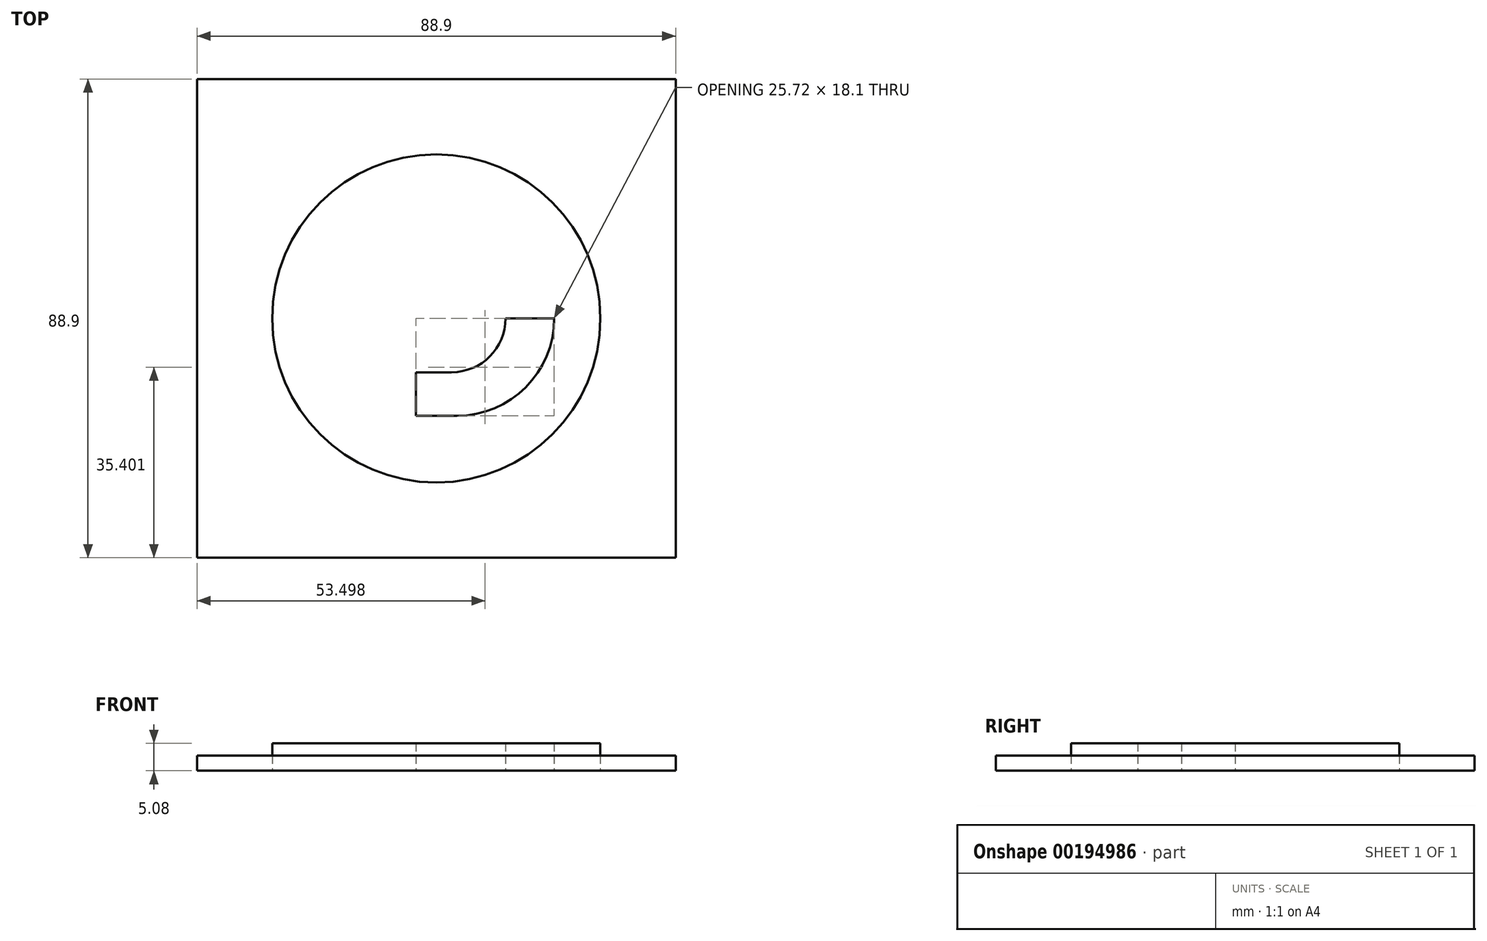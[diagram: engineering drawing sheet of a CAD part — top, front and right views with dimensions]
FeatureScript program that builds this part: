
annotation { "Feature Type Name" : "Feature", "Feature Type Description" : "" }
export const myFeature = defineFeature(function(context is Context, id is Id, definition is map)
    precondition{}
    {
        {
            var Q0;
            Q0=qCreatedBy(makeId("Top.planeOp"),FACE);
            var sketch = newSketch(context, id + "F0", { "sketchPlane" : qUnion([Q0])});
            skCircle(sketch, "E0", {"center": v(-1.1, 0) * mm, "radius": 38.1 * mm});
            skCircle(sketch, "E1", {"center": v(-1.1, 0) * mm, "radius": 30.48 * mm});
            skLineSegment(sketch, "E2", {"start": v(-4.91, -18.1) * mm, "end": v(-4.91, 7.14) * mm});
            skLineSegment(sketch, "E3", {"start": v(-4.91, 7.14) * mm, "end": v(-13, 7.14) * mm});
            skLineSegment(sketch, "E4", {"start": v(-13, 7.14) * mm, "end": v(-13, -18.1) * mm});
            skLineSegment(sketch, "E5", {"start": v(-13, -18.1) * mm, "end": v(-4.91, -18.1) * mm});
            skArc(sketch, "E6", {"start": v(20.8, 0) * mm, "mid": v(15.5, -12.8) * mm, "end": v(2.7, -18.1) * mm});
            skLineSegment(sketch, "E7", {"start": v(2.7, -18.1) * mm, "end": v(-4.91, -18.1) * mm});
            skLineSegment(sketch, "E8", {"start": v(-4.91, -18.1) * mm, "end": v(-4.91, -10) * mm});
            skLineSegment(sketch, "E9", {"start": v(-4.91, -10) * mm, "end": v(1.76, -10) * mm});
            skArc(sketch, "E10", {"start": v(1.76, -10) * mm, "mid": v(8.83, -7.07) * mm, "end": v(11.76, 0) * mm});
            skLineSegment(sketch, "E11", {"start": v(11.76, 0) * mm, "end": v(20.8, 0) * mm});
            skArc(sketch, "E12", {"start": v(20.8, 0) * mm, "mid": v(15.5, 12.8) * mm, "end": v(2.7, 18.1) * mm});
            skLineSegment(sketch, "E13", {"start": v(2.7, 18.1) * mm, "end": v(-22.06, 18.1) * mm});
            skLineSegment(sketch, "E14", {"start": v(-22.06, 18.1) * mm, "end": v(-22.06, 10) * mm});
            skLineSegment(sketch, "E15", {"start": v(-22.06, 10) * mm, "end": v(1.76, 10) * mm});
            skArc(sketch, "E16", {"start": v(1.76, 10) * mm, "mid": v(8.83, 7.07) * mm, "end": v(11.76, 0) * mm});
            skSolve(sketch);
        }
        {
            var Q0;
            Q0=makeQuery(id+"F0.imprint","IMPRINT",FACE,{"disambiguationData":[TD([[makeQuery(id+"F0.imprint","IMPRINT",EDGE,{"derivedFrom":sQuery(id+"F0.wireOp",EDGE,"E2")}),1.0]])]});
            var Q1;
            Q1=makeQuery(id+"F0.imprint","IMPRINT",FACE,{"disambiguationData":[TD([[makeQuery(id+"F0.imprint","IMPRINT",EDGE,{"derivedFrom":sQuery(id+"F0.wireOp",EDGE,"E12")}),1.0]])]});
            var Q2;
            Q2=makeQuery(id+"F0.imprint","IMPRINT",FACE,{"disambiguationData":[TD([[makeQuery(id+"F0.imprint","IMPRINT",EDGE,{"derivedFrom":sQuery(id+"F0.wireOp",EDGE,"E6")}),-1.0]])]});
            var Q3;
            Q3=makeQuery(id+"F0.imprint","IMPRINT",FACE,{"disambiguationData":[TD([[makeQuery(id+"F0.imprint","IMPRINT",EDGE,{"derivedFrom":sQuery(id+"F0.wireOp",EDGE,"E0")}),-1.0]])]});
            extrude(context, id + "F1", {"entities" : qUnion([Q0, Q1, Q2, Q3]), "depth" : 5.08 * mm});
        }
        {
            var Q0;
            Q0=qCreatedBy(makeId("Top.planeOp"),FACE);
            var sketch = newSketch(context, id + "F2", { "sketchPlane" : qUnion([Q0])});
            skLineSegment(sketch, "E17.bottom", {"start": v(-45.55, -44.45) * mm, "end": v(43.35, -44.45) * mm});
            skLineSegment(sketch, "E17.top", {"start": v(-45.55, 44.45) * mm, "end": v(43.35, 44.45) * mm});
            skLineSegment(sketch, "E17.left", {"start": v(-45.55, -44.45) * mm, "end": v(-45.55, 44.45) * mm});
            skLineSegment(sketch, "E17.right", {"start": v(43.35, -44.45) * mm, "end": v(43.35, 44.45) * mm});
            skSolve(sketch);
        }
        {
            var Q0;
            Q0=makeQuery(id+"F2.imprint","IMPRINT",FACE,{"disambiguationData":[TD([[makeQuery(id+"F2.imprint","IMPRINT",EDGE,{"derivedFrom":sQuery(id+"F2.wireOp",EDGE,"E17.bottom")}),1.0]])]});
            extrude(context, id + "F3", {"entities" : qUnion([Q0]), "depth" : 2.8 * mm});
        }
    });
